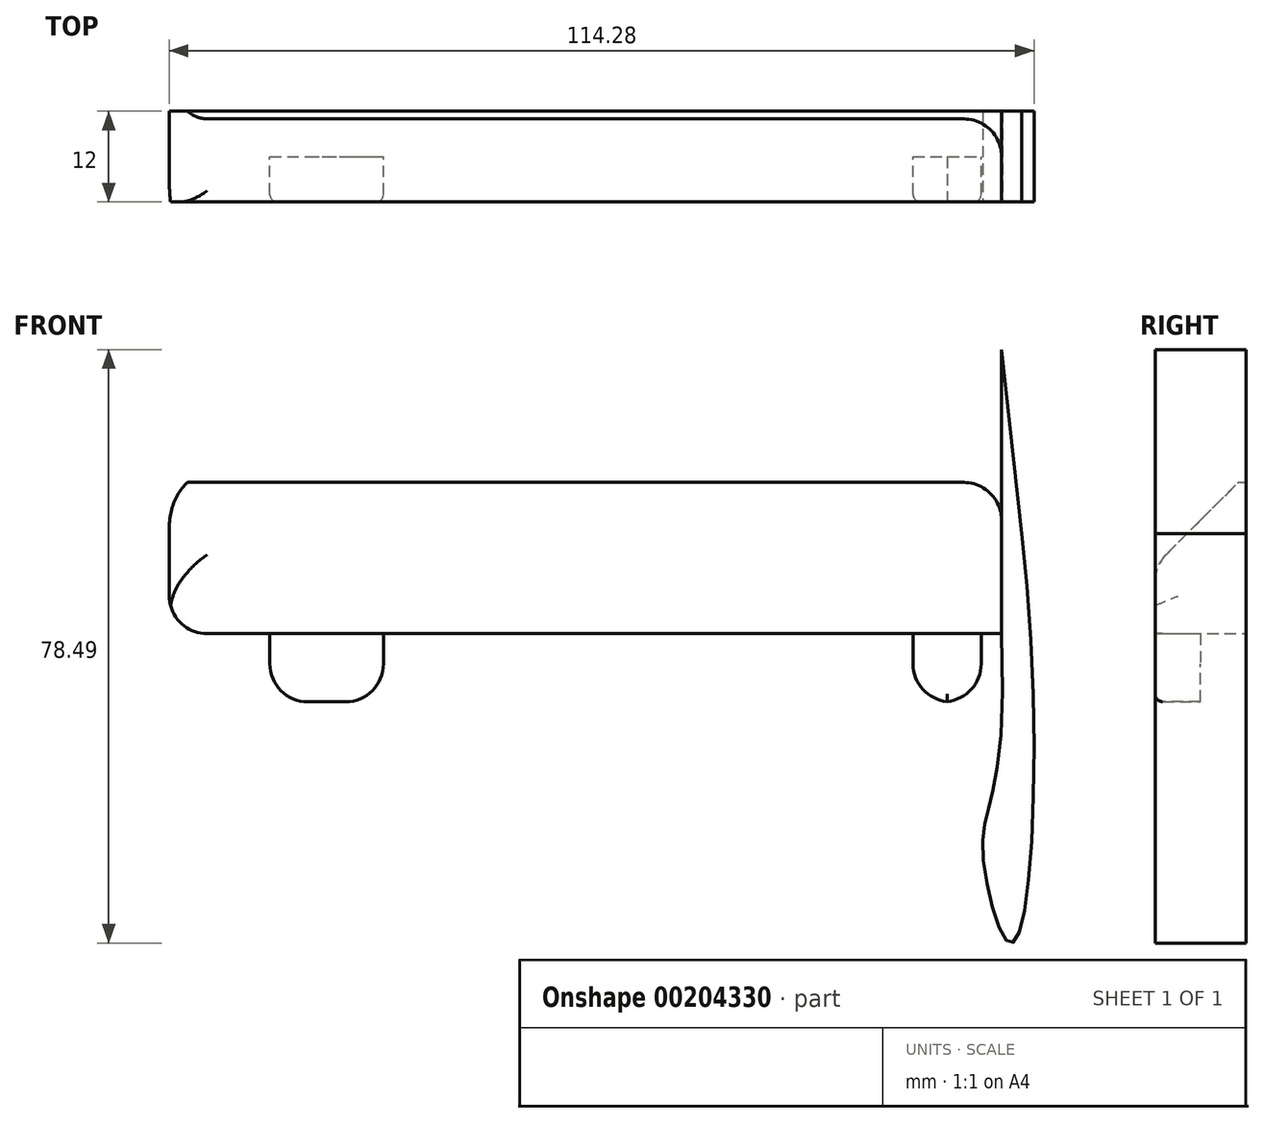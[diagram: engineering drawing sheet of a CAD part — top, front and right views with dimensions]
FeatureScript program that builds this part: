
annotation { "Feature Type Name" : "Feature", "Feature Type Description" : "" }
export const myFeature = defineFeature(function(context is Context, id is Id, definition is map)
    precondition{}
    {
        {
            var Q0;
            Q0=qCreatedBy(makeId("Front.planeOp"),FACE);
            var sketch = newSketch(context, id + "F0", { "sketchPlane" : qUnion([Q0])});
            skLineSegment(sketch, "E0", {"start": v(-34.63, -6.47) * mm, "end": v(75.37, -6.47) * mm});
            skLineSegment(sketch, "E1", {"start": v(75.37, -6.47) * mm, "end": v(75.37, 13.53) * mm});
            skLineSegment(sketch, "E2", {"start": v(75.37, 13.53) * mm, "end": v(-34.63, 13.53) * mm});
            skLineSegment(sketch, "E3", {"start": v(-21.33, -6.47) * mm, "end": v(-21.33, -15.47) * mm});
            skLineSegment(sketch, "E4", {"start": v(-21.33, -15.47) * mm, "end": v(-6.33, -15.47) * mm});
            skLineSegment(sketch, "E5", {"start": v(-6.33, -15.47) * mm, "end": v(-6.33, -6.47) * mm});
            skLineSegment(sketch, "E6", {"start": v(72.67, -6.47) * mm, "end": v(72.67, -15.47) * mm});
            skLineSegment(sketch, "E7", {"start": v(63.67, -15.47) * mm, "end": v(72.67, -15.47) * mm});
            skLineSegment(sketch, "E8", {"start": v(63.67, -15.47) * mm, "end": v(63.67, -6.47) * mm});
            skLineSegment(sketch, "E9.bottom", {"start": v(-16.83, -6.47) * mm, "end": v(-10.83, -6.47) * mm});
            skLineSegment(sketch, "E9.top", {"start": v(-16.83, -15.47) * mm, "end": v(-10.83, -15.47) * mm});
            skLineSegment(sketch, "E9.left", {"start": v(-16.83, -6.47) * mm, "end": v(-16.83, -15.47) * mm});
            skLineSegment(sketch, "E9.right", {"start": v(-10.83, -6.47) * mm, "end": v(-10.83, -15.47) * mm});
            skLineSegment(sketch, "E10.bottom", {"start": v(65.17, -6.47) * mm, "end": v(71.17, -6.47) * mm});
            skLineSegment(sketch, "E10.top", {"start": v(65.17, -15.47) * mm, "end": v(71.17, -15.47) * mm});
            skLineSegment(sketch, "E10.left", {"start": v(65.17, -6.47) * mm, "end": v(65.17, -15.47) * mm});
            skLineSegment(sketch, "E10.right", {"start": v(71.17, -6.47) * mm, "end": v(71.17, -15.47) * mm});
            skLineSegment(sketch, "E11.bottom", {"start": v(-21.33, -6.47) * mm, "end": v(-6.33, -6.47) * mm});
            skLineSegment(sketch, "E11.top", {"start": v(-21.33, -10.67) * mm, "end": v(-6.33, -10.67) * mm});
            skLineSegment(sketch, "E11.left", {"start": v(-21.33, -6.47) * mm, "end": v(-21.33, -10.67) * mm});
            skLineSegment(sketch, "E11.right", {"start": v(-6.33, -6.47) * mm, "end": v(-6.33, -10.67) * mm});
            skLineSegment(sketch, "E12.bottom", {"start": v(63.67, -6.47) * mm, "end": v(72.67, -6.47) * mm});
            skLineSegment(sketch, "E12.top", {"start": v(63.67, -10.67) * mm, "end": v(72.67, -10.67) * mm});
            skLineSegment(sketch, "E12.left", {"start": v(63.67, -6.47) * mm, "end": v(63.67, -10.67) * mm});
            skLineSegment(sketch, "E12.right", {"start": v(72.67, -6.47) * mm, "end": v(72.67, -10.67) * mm});
            skFitSpline(sketch, "E13", {"points": [v(75.37, 13.53) * mm, v(78.02, 6.78) * mm, v(76.56, -47.38) * mm, v(72.89, -35.3) * mm, v(75.37, -6.47) * mm], "startDerivative": vector(0, 198.72) * mm, "endDerivative": vector(-9.37, 234.27) * mm});
            skLineSegment(sketch, "E14", {"start": v(-34.63, 13.53) * mm, "end": v(-34.63, -6.47) * mm});
            skLineSegment(sketch, "E15.bottom", {"start": v(55.37, 13.53) * mm, "end": v(75.37, 13.53) * mm});
            skLineSegment(sketch, "E15.top", {"start": v(55.37, 53.53) * mm, "end": v(75.37, 53.53) * mm});
            skLineSegment(sketch, "E15.left", {"start": v(55.37, 13.53) * mm, "end": v(55.37, 53.53) * mm});
            skLineSegment(sketch, "E15.right", {"start": v(75.37, 13.53) * mm, "end": v(75.37, 53.53) * mm});
            skFitSpline(sketch, "E16", {"points": [v(78.02, 6.78) * mm, v(75.37, 31.1) * mm], "startDerivative": vector(-2.65, 24.33) * mm, "endDerivative": vector(-2.65, 24.33) * mm});
            skSolve(sketch);
        }
        {
            var Q0;
            {var subQ4=sQuery(id+"F0.wireOp",EDGE,"jVZ0xt1w-W0Ll-cNEo-aC1z-4cyqBLWAK3kW");Q0=makeQuery(id+"F0.imprint","IMPRINT",FACE,{"disambiguationData":[TD([[makeQuery(id+"F0.imprint","IMPRINT",EDGE,{"derivedFrom":subQ4}),1.0]])]});}
            var Q1;
            {var subQ0=sQuery(id+"F0.wireOp",EDGE,"E3");Q1=makeQuery(id+"F0.imprint","IMPRINT",FACE,{"disambiguationData":[TD([[makeQuery(id+"F0.imprint","IMPRINT",EDGE,{"derivedFrom":subQ0}),1.0]])]});}
            var Q2;
            {var subQ0=sQuery(id+"F0.wireOp",EDGE,"E6");Q2=makeQuery(id+"F0.imprint","IMPRINT",FACE,{"disambiguationData":[TD([[makeQuery(id+"F0.imprint","IMPRINT",EDGE,{"derivedFrom":subQ0}),-1.0]])]});}
            var Q3;
            Q3=makeQuery(id+"F0.imprint","IMPRINT",FACE,{"disambiguationData":[TD([[makeQuery(id+"F0.imprint","IMPRINT",EDGE,{"derivedFrom":sQuery(id+"F0.wireOp",EDGE,"E9.bottom")}),-1.0]])]});
            var Q4;
            Q4=makeQuery(id+"F0.imprint","IMPRINT",FACE,{"disambiguationData":[TD([[makeQuery(id+"F0.imprint","IMPRINT",EDGE,{"derivedFrom":sQuery(id+"F0.wireOp",EDGE,"E10.bottom")}),-1.0]])]});
            var Q5;
            {var subQ0=sQuery(id+"F0.wireOp",EDGE,"E5");Q5=makeQuery(id+"F0.imprint","IMPRINT",FACE,{"disambiguationData":[TD([[makeQuery(id+"F0.imprint","IMPRINT",EDGE,{"derivedFrom":subQ0}),1.0]])]});}
            var Q6;
            {var subQ0=sQuery(id+"F0.wireOp",EDGE,"E8");Q6=makeQuery(id+"F0.imprint","IMPRINT",FACE,{"disambiguationData":[TD([[makeQuery(id+"F0.imprint","IMPRINT",EDGE,{"derivedFrom":subQ0}),-1.0]])]});}
            var Q7;
            {var subQ0=sQuery(id+"F0.wireOp",EDGE,"E11.bottom");var subQ1=sQuery(id+"F0.wireOp",EDGE,"E9.left");var subQ2=makeQuery(id+"F0.imprint","INTERSECT",VERTEX,{"derivedFrom":[subQ1,subQ0]});Q7=makeQuery(id+"F0.imprint","IMPRINT",FACE,{"disambiguationData":[TD([[makeQuery(id+"F0.imprint","IMPRINT",EDGE,{"disambiguationData":[TD([[subQ2,-1.0]])],"derivedFrom":subQ1}),1.0]])]});}
            var Q8;
            {var subQ0=sQuery(id+"F0.wireOp",EDGE,"E9.top");Q8=makeQuery(id+"F0.imprint","IMPRINT",FACE,{"disambiguationData":[TD([[makeQuery(id+"F0.imprint","IMPRINT",EDGE,{"derivedFrom":subQ0}),1.0]])]});}
            var Q9;
            {var subQ5=sQuery(id+"F0.wireOp",EDGE,"E11.right");Q9=makeQuery(id+"F0.imprint","IMPRINT",FACE,{"disambiguationData":[TD([[makeQuery(id+"F0.imprint","IMPRINT",EDGE,{"derivedFrom":subQ5}),-1.0]])]});}
            var Q10;
            {var subQ5=sQuery(id+"F0.wireOp",EDGE,"E11.left");Q10=makeQuery(id+"F0.imprint","IMPRINT",FACE,{"disambiguationData":[TD([[makeQuery(id+"F0.imprint","IMPRINT",EDGE,{"derivedFrom":subQ5}),1.0]])]});}
            var Q11;
            {var subQ0=sQuery(id+"F0.wireOp",EDGE,"E12.bottom");var subQ1=sQuery(id+"F0.wireOp",EDGE,"E10.left");var subQ2=makeQuery(id+"F0.imprint","INTERSECT",VERTEX,{"derivedFrom":[subQ1,subQ0]});Q11=makeQuery(id+"F0.imprint","IMPRINT",FACE,{"disambiguationData":[TD([[makeQuery(id+"F0.imprint","IMPRINT",EDGE,{"disambiguationData":[TD([[subQ2,-1.0]])],"derivedFrom":subQ1}),1.0]])]});}
            var Q12;
            {var subQ0=sQuery(id+"F0.wireOp",EDGE,"E10.top");Q12=makeQuery(id+"F0.imprint","IMPRINT",FACE,{"disambiguationData":[TD([[makeQuery(id+"F0.imprint","IMPRINT",EDGE,{"derivedFrom":subQ0}),1.0]])]});}
            var Q13;
            {var subQ5=sQuery(id+"F0.wireOp",EDGE,"E12.right");Q13=makeQuery(id+"F0.imprint","IMPRINT",FACE,{"disambiguationData":[TD([[makeQuery(id+"F0.imprint","IMPRINT",EDGE,{"derivedFrom":subQ5}),-1.0]])]});}
            var Q14;
            {var subQ5=sQuery(id+"F0.wireOp",EDGE,"E12.left");Q14=makeQuery(id+"F0.imprint","IMPRINT",FACE,{"disambiguationData":[TD([[makeQuery(id+"F0.imprint","IMPRINT",EDGE,{"derivedFrom":subQ5}),1.0]])]});}
            var Q15;
            Q15=makeQuery(id+"F0.imprint","IMPRINT",FACE,{"disambiguationData":[TD([[makeQuery(id+"F0.imprint","IMPRINT",EDGE,{"derivedFrom":sQuery(id+"F0.wireOp",EDGE,"E1")}),-1.0]])]});
            var Q16;
            {var subQ3=sQuery(id+"F0.wireOp",EDGE,"E16");Q16=makeQuery(id+"F0.imprint","IMPRINT",FACE,{"disambiguationData":[TD([[makeQuery(id+"F0.imprint","IMPRINT",EDGE,{"derivedFrom":subQ3}),1.0]])]});}
            extrude(context, id + "F1", {"entities" : qUnion([Q0, Q1, Q2, Q3, Q4, Q5, Q6, Q7, Q8, Q9, Q10, Q11, Q12, Q13, Q14, Q15, Q16]), "depth" : 12 * mm});
        }
        {
            var Q0;
            {var subQ0=sQuery(id+"F0.wireOp",EDGE,"E9.top");Q0=makeQuery(id+"F0.imprint","IMPRINT",FACE,{"disambiguationData":[TD([[makeQuery(id+"F0.imprint","IMPRINT",EDGE,{"derivedFrom":subQ0}),1.0]])]});}
            var Q1;
            {var subQ0=sQuery(id+"F0.wireOp",EDGE,"E12.bottom");var subQ1=sQuery(id+"F0.wireOp",EDGE,"E10.left");var subQ2=makeQuery(id+"F0.imprint","INTERSECT",VERTEX,{"derivedFrom":[subQ1,subQ0]});Q1=makeQuery(id+"F0.imprint","IMPRINT",FACE,{"disambiguationData":[TD([[makeQuery(id+"F0.imprint","IMPRINT",EDGE,{"disambiguationData":[TD([[subQ2,-1.0]])],"derivedFrom":subQ1}),1.0]])]});}
            var Q2;
            {var subQ0=sQuery(id+"F0.wireOp",EDGE,"E11.bottom");var subQ1=sQuery(id+"F0.wireOp",EDGE,"E9.left");var subQ2=makeQuery(id+"F0.imprint","INTERSECT",VERTEX,{"derivedFrom":[subQ1,subQ0]});Q2=makeQuery(id+"F0.imprint","IMPRINT",FACE,{"disambiguationData":[TD([[makeQuery(id+"F0.imprint","IMPRINT",EDGE,{"disambiguationData":[TD([[subQ2,-1.0]])],"derivedFrom":subQ1}),1.0]])]});}
            var Q3;
            {var subQ5=sQuery(id+"F0.wireOp",EDGE,"E11.left");Q3=makeQuery(id+"F0.imprint","IMPRINT",FACE,{"disambiguationData":[TD([[makeQuery(id+"F0.imprint","IMPRINT",EDGE,{"derivedFrom":subQ5}),1.0]])]});}
            var Q4;
            {var subQ5=sQuery(id+"F0.wireOp",EDGE,"E11.right");Q4=makeQuery(id+"F0.imprint","IMPRINT",FACE,{"disambiguationData":[TD([[makeQuery(id+"F0.imprint","IMPRINT",EDGE,{"derivedFrom":subQ5}),-1.0]])]});}
            var Q5;
            {var subQ5=sQuery(id+"F0.wireOp",EDGE,"E12.left");Q5=makeQuery(id+"F0.imprint","IMPRINT",FACE,{"disambiguationData":[TD([[makeQuery(id+"F0.imprint","IMPRINT",EDGE,{"derivedFrom":subQ5}),1.0]])]});}
            var Q6;
            {var subQ5=sQuery(id+"F0.wireOp",EDGE,"E12.right");Q6=makeQuery(id+"F0.imprint","IMPRINT",FACE,{"disambiguationData":[TD([[makeQuery(id+"F0.imprint","IMPRINT",EDGE,{"derivedFrom":subQ5}),-1.0]])]});}
            var Q7;
            {var subQ0=sQuery(id+"F0.wireOp",EDGE,"E5");Q7=makeQuery(id+"F0.imprint","IMPRINT",FACE,{"disambiguationData":[TD([[makeQuery(id+"F0.imprint","IMPRINT",EDGE,{"derivedFrom":subQ0}),1.0]])]});}
            var Q8;
            {var subQ0=sQuery(id+"F0.wireOp",EDGE,"E3");Q8=makeQuery(id+"F0.imprint","IMPRINT",FACE,{"disambiguationData":[TD([[makeQuery(id+"F0.imprint","IMPRINT",EDGE,{"derivedFrom":subQ0}),1.0]])]});}
            var Q9;
            {var subQ0=sQuery(id+"F0.wireOp",EDGE,"E10.top");Q9=makeQuery(id+"F0.imprint","IMPRINT",FACE,{"disambiguationData":[TD([[makeQuery(id+"F0.imprint","IMPRINT",EDGE,{"derivedFrom":subQ0}),1.0]])]});}
            var Q10;
            {var subQ0=sQuery(id+"F0.wireOp",EDGE,"E8");Q10=makeQuery(id+"F0.imprint","IMPRINT",FACE,{"disambiguationData":[TD([[makeQuery(id+"F0.imprint","IMPRINT",EDGE,{"derivedFrom":subQ0}),-1.0]])]});}
            var Q11;
            {var subQ0=sQuery(id+"F0.wireOp",EDGE,"E6");Q11=makeQuery(id+"F0.imprint","IMPRINT",FACE,{"disambiguationData":[TD([[makeQuery(id+"F0.imprint","IMPRINT",EDGE,{"derivedFrom":subQ0}),-1.0]])]});}
            extrude(context, id + "F2", {"entities" : qUnion([Q0, Q1, Q2, Q3, Q4, Q5, Q6, Q7, Q8, Q9, Q10, Q11]), "operationType" : NewBodyOperationType.REMOVE, "depth" : 6 * mm});
        }
        {
            var Q0;
            {var subQ12=sQuery(id+"F0.wireOp",EDGE,"E1");Q0=makeQuery(id+"F0.imprint","IMPRINT",FACE,{"disambiguationData":[TD([[makeQuery(id+"F0.imprint","IMPRINT",EDGE,{"derivedFrom":subQ12}),1.0]])]});}
            var Q1;
            Q1=makeQuery(id+"F0.imprint","IMPRINT",FACE,{"disambiguationData":[TD([[makeQuery(id+"F0.imprint","IMPRINT",EDGE,{"derivedFrom":sQuery(id+"F0.wireOp",EDGE,"E15.bottom")}),1.0]])]});
            extrude(context, id + "F3", {"entities" : qUnion([Q0, Q1]), "depth" : 12 * mm});
        }
        {
            var Q0;
            Q0=makeQuery(id+"F3.opExtrude","CAP_EDGE",EDGE,{"disambiguationData":[OSD([sQuery(id+"F0.wireOp",EDGE,"E2")])],"isStart":false});
            var Q1;
            Q1=makeQuery(id+"F3.opExtrude","CAP_EDGE",EDGE,{"disambiguationData":[OSD([sQuery(id+"F0.wireOp",EDGE,"E15.left")])],"isStart":false});
            chamfer(context, id + "F4", {"entities" : qUnion([Q0, Q1]), "width" : 11 * mm, "tangentPropagation" : true});
        }
        {
            var Q0;
            {var subQ0=sQuery(id+"F0.wireOp",EDGE,"E2");Q0=makeQuery(id+"F4.opChamfer","BLEND_EDGE",EDGE,{"blendedFrom":[makeQuery(id+"F3.opExtrude","CAP_EDGE",EDGE,{"disambiguationData":[OSD([subQ0])],"isStart":false}),makeQuery(id+"F3.opExtrude","CAP_FACE",FACE,{"disambiguationData":[OSD([sQuery(id+"F0.wireOp",EDGE,"E0"),sQuery(id+"F0.wireOp",EDGE,"E1"),subQ0,sQuery(id+"F0.wireOp",EDGE,"E11.bottom"),sQuery(id+"F0.wireOp",EDGE,"E12.bottom"),sQuery(id+"F0.wireOp",EDGE,"E14"),sQuery(id+"F0.wireOp",EDGE,"E15.top"),sQuery(id+"F0.wireOp",EDGE,"E15.left"),sQuery(id+"F0.wireOp",EDGE,"E15.right")])],"isStart":false})],"blendedInto":[makeQuery(id+"F3.opExtrude","CAP_FACE",FACE,{"disambiguationData":[OSD([sQuery(id+"F0.wireOp",EDGE,"E0"),sQuery(id+"F0.wireOp",EDGE,"E1"),subQ0,sQuery(id+"F0.wireOp",EDGE,"E11.bottom"),sQuery(id+"F0.wireOp",EDGE,"E12.bottom"),sQuery(id+"F0.wireOp",EDGE,"E14"),sQuery(id+"F0.wireOp",EDGE,"E15.top"),sQuery(id+"F0.wireOp",EDGE,"E15.left"),sQuery(id+"F0.wireOp",EDGE,"E15.right")])],"isStart":false})]});}
            var Q1;
            Q1=makeQuery(id+"F4.opChamfer","BLEND_EDGE",EDGE,{"blendedFrom":[makeQuery(id+"F3.opExtrude","CAP_EDGE",EDGE,{"disambiguationData":[OSD([sQuery(id+"F0.wireOp",EDGE,"E2")])],"isStart":false}),makeQuery(id+"F3.opExtrude","SWEPT_FACE",FACE,{"disambiguationData":[OSD([sQuery(id+"F0.wireOp",EDGE,"E14")])]})],"blendedInto":[makeQuery(id+"F3.opExtrude","SWEPT_FACE",FACE,{"disambiguationData":[OSD([sQuery(id+"F0.wireOp",EDGE,"E14")])]})]});
            var Q2;
            Q2=makeQuery(id+"F3.opExtrude","SWEPT_EDGE",EDGE,{"disambiguationData":[OSD([sQuery(id+"F0.wireOp",EDGE,"E0"),sQuery(id+"F0.wireOp",EDGE,"E14")])]});
            var Q3;
            Q3=makeQuery(id+"F4.opChamfer","BLEND_EDGE",EDGE,{"blendedFrom":[makeQuery(id+"F3.opExtrude","CAP_EDGE",EDGE,{"disambiguationData":[OSD([sQuery(id+"F0.wireOp",EDGE,"E15.left")])],"isStart":false}),makeQuery(id+"F3.opExtrude","SWEPT_FACE",FACE,{"disambiguationData":[OSD([sQuery(id+"F0.wireOp",EDGE,"E15.top")])]})],"blendedInto":[makeQuery(id+"F3.opExtrude","SWEPT_FACE",FACE,{"disambiguationData":[OSD([sQuery(id+"F0.wireOp",EDGE,"E15.top")])]})]});
            var Q4;
            Q4=makeQuery(id+"F4.opChamfer","BLEND_EDGE",EDGE,{"blendedFrom":[makeQuery(id+"F3.opExtrude","CAP_EDGE",EDGE,{"disambiguationData":[OSD([sQuery(id+"F0.wireOp",EDGE,"E2")])],"isStart":false}),makeQuery(id+"F3.opExtrude","CAP_EDGE",EDGE,{"disambiguationData":[OSD([sQuery(id+"F0.wireOp",EDGE,"E15.left")])],"isStart":false})],"blendedInto":[]});
            var Q5;
            Q5=makeQuery(id+"F3.opExtrude","SWEPT_EDGE",EDGE,{"disambiguationData":[OSD([sQuery(id+"F0.wireOp",EDGE,"E15.top"),sQuery(id+"F0.wireOp",EDGE,"E15.right")])]});
            fillet(context, id + "F5", {"entities" : qUnion([Q0, Q1, Q2, Q3, Q4, Q5]), "radius" : 5 * mm, "tangentPropagation" : true, "allowEdgeOverflow" : false});
        }
        {
            var Q0;
            Q0=makeQuery(id+"F1.opExtrude","SWEPT_EDGE",EDGE,{"disambiguationData":[OSD([sQuery(id+"F0.wireOp",EDGE,"E3"),sQuery(id+"F0.wireOp",EDGE,"E4")])]});
            var Q1;
            Q1=makeQuery(id+"F1.opExtrude","SWEPT_EDGE",EDGE,{"disambiguationData":[OSD([sQuery(id+"F0.wireOp",EDGE,"E4"),sQuery(id+"F0.wireOp",EDGE,"E5")])]});
            var Q2;
            Q2=makeQuery(id+"F1.opExtrude","SWEPT_EDGE",EDGE,{"disambiguationData":[OSD([sQuery(id+"F0.wireOp",EDGE,"E7"),sQuery(id+"F0.wireOp",EDGE,"E8")])]});
            var Q3;
            Q3=makeQuery(id+"F1.opExtrude","SWEPT_EDGE",EDGE,{"disambiguationData":[OSD([sQuery(id+"F0.wireOp",EDGE,"E6"),sQuery(id+"F0.wireOp",EDGE,"E7")])]});
            fillet(context, id + "F6", {"entities" : qUnion([Q0, Q1, Q2, Q3]), "radius" : 5 * mm, "tangentPropagation" : true, "allowEdgeOverflow" : false});
        }
        {
            var Q0;
            {var subQ0=sQuery(id+"F0.wireOp",EDGE,"E7");var subQ1=sQuery(id+"F0.wireOp",EDGE,"E6");Q0=makeQuery(id+"F6.opFillet","BLEND_EDGE",EDGE,{"blendedFrom":[makeQuery(id+"F1.opExtrude","SWEPT_EDGE",EDGE,{"disambiguationData":[OSD([subQ1,subQ0])]}),makeQuery(id+"F1.opExtrude","CAP_FACE",FACE,{"disambiguationData":[OSD([subQ1,subQ0,sQuery(id+"F0.wireOp",EDGE,"E8"),sQuery(id+"F0.wireOp",EDGE,"E10.top"),sQuery(id+"F0.wireOp",EDGE,"E12.bottom"),sQuery(id+"F0.wireOp",EDGE,"E12.left"),sQuery(id+"F0.wireOp",EDGE,"E12.right")])],"isStart":false})],"blendedInto":[makeQuery(id+"F1.opExtrude","CAP_FACE",FACE,{"disambiguationData":[OSD([subQ1,subQ0,sQuery(id+"F0.wireOp",EDGE,"E8"),sQuery(id+"F0.wireOp",EDGE,"E10.top"),sQuery(id+"F0.wireOp",EDGE,"E12.bottom"),sQuery(id+"F0.wireOp",EDGE,"E12.left"),sQuery(id+"F0.wireOp",EDGE,"E12.right")])],"isStart":false})]});}
            var Q1;
            {var subQ0=sQuery(id+"F0.wireOp",EDGE,"E8");var subQ1=sQuery(id+"F0.wireOp",EDGE,"E7");Q1=makeQuery(id+"F6.opFillet","BLEND_EDGE",EDGE,{"blendedFrom":[makeQuery(id+"F1.opExtrude","SWEPT_EDGE",EDGE,{"disambiguationData":[OSD([subQ1,subQ0])]}),makeQuery(id+"F1.opExtrude","CAP_FACE",FACE,{"disambiguationData":[OSD([sQuery(id+"F0.wireOp",EDGE,"E6"),subQ1,subQ0,sQuery(id+"F0.wireOp",EDGE,"E10.top"),sQuery(id+"F0.wireOp",EDGE,"E12.bottom"),sQuery(id+"F0.wireOp",EDGE,"E12.left"),sQuery(id+"F0.wireOp",EDGE,"E12.right")])],"isStart":false})],"blendedInto":[makeQuery(id+"F1.opExtrude","CAP_FACE",FACE,{"disambiguationData":[OSD([sQuery(id+"F0.wireOp",EDGE,"E6"),subQ1,subQ0,sQuery(id+"F0.wireOp",EDGE,"E10.top"),sQuery(id+"F0.wireOp",EDGE,"E12.bottom"),sQuery(id+"F0.wireOp",EDGE,"E12.left"),sQuery(id+"F0.wireOp",EDGE,"E12.right")])],"isStart":false})]});}
            var Q2;
            {var subQ0=sQuery(id+"F0.wireOp",EDGE,"E5");var subQ1=sQuery(id+"F0.wireOp",EDGE,"E4");Q2=makeQuery(id+"F6.opFillet","BLEND_EDGE",EDGE,{"blendedFrom":[makeQuery(id+"F1.opExtrude","SWEPT_EDGE",EDGE,{"disambiguationData":[OSD([subQ1,subQ0])]}),makeQuery(id+"F1.opExtrude","CAP_FACE",FACE,{"disambiguationData":[OSD([sQuery(id+"F0.wireOp",EDGE,"E3"),subQ1,subQ0,sQuery(id+"F0.wireOp",EDGE,"E9.top"),sQuery(id+"F0.wireOp",EDGE,"E11.bottom"),sQuery(id+"F0.wireOp",EDGE,"E11.left"),sQuery(id+"F0.wireOp",EDGE,"E11.right")])],"isStart":false})],"blendedInto":[makeQuery(id+"F1.opExtrude","CAP_FACE",FACE,{"disambiguationData":[OSD([sQuery(id+"F0.wireOp",EDGE,"E3"),subQ1,subQ0,sQuery(id+"F0.wireOp",EDGE,"E9.top"),sQuery(id+"F0.wireOp",EDGE,"E11.bottom"),sQuery(id+"F0.wireOp",EDGE,"E11.left"),sQuery(id+"F0.wireOp",EDGE,"E11.right")])],"isStart":false})]});}
            fillet(context, id + "F7", {"entities" : qUnion([Q0, Q1, Q2]), "radius" : 1 * mm, "tangentPropagation" : true, "allowEdgeOverflow" : false});
        }
    });
